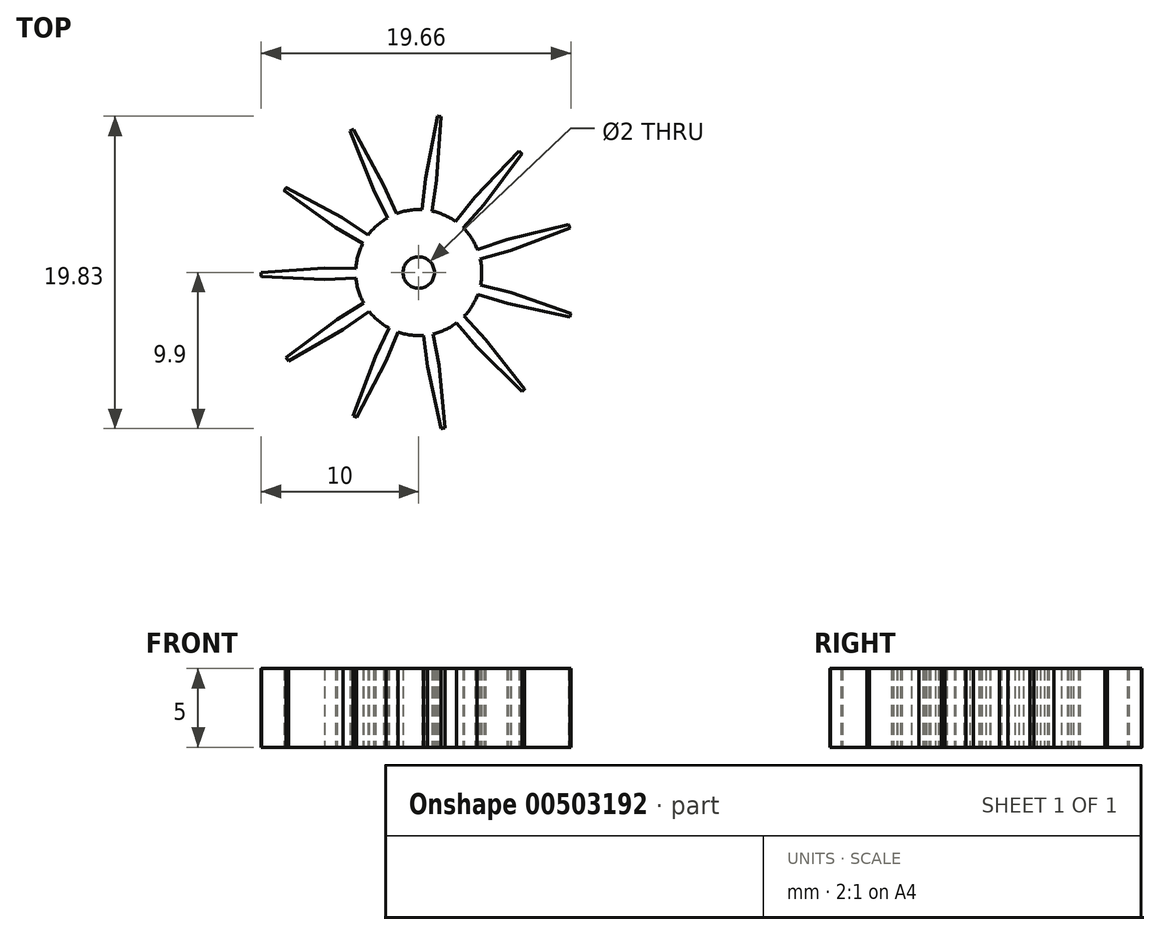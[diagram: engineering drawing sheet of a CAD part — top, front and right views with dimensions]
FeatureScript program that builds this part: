
annotation { "Feature Type Name" : "Feature", "Feature Type Description" : "" }
export const myFeature = defineFeature(function(context is Context, id is Id, definition is map)
    precondition{}
    {
        {
            var Q0;
            Q0=qCreatedBy(makeId("Top.planeOp"),FACE);
            var sketch = newSketch(context, id + "F0", { "sketchPlane" : qUnion([Q0])});
            skCircle(sketch, "E0", {"center": v(0, 0) * mm, "radius": 1 * mm});
            skArc(sketch, "E1", {"start": v(1.14, 5.89) * mm, "mid": v(0.78, 5.95) * mm, "end": v(0.42, 5.99) * mm, "construction": true});
            skArc(sketch, "E2", {"start": v(1.43, 9.9) * mm, "mid": v(1.3, 9.91) * mm, "end": v(1.19, 9.93) * mm});
            skCircle(sketch, "E3", {"center": v(0, 0) * mm, "radius": 4 * mm});
            skLineSegment(sketch, "E4", {"start": v(0, 0) * mm, "end": v(0, 7.63) * mm, "construction": true});
            skLineSegment(sketch, "E5", {"start": v(0, 0) * mm, "end": v(2.03, 7.58) * mm, "construction": true});
            skLineSegment(sketch, "E6", {"start": v(0.42, 5.99) * mm, "end": v(0.2, 4) * mm});
            skLineSegment(sketch, "E7", {"start": v(1.19, 9.93) * mm, "end": v(0.42, 5.99) * mm});
            skLineSegment(sketch, "E8", {"start": v(1.43, 9.9) * mm, "end": v(1.14, 5.89) * mm});
            skLineSegment(sketch, "E9", {"start": v(1.14, 5.89) * mm, "end": v(0.83, 3.91) * mm});
            skLineSegment(sketch, "E10", {"start": v(0.33, 6.33) * mm, "end": v(0, 0) * mm, "construction": true});
            skLineSegment(sketch, "E11", {"start": v(0, 0) * mm, "end": v(1.34, 6.3) * mm, "construction": true});
            skSolve(sketch);
        }
        {
            var Q0;
            Q0=makeQuery(id+"F0.imprint","IMPRINT",FACE,{"disambiguationData":[TD([[makeQuery(id+"F0.imprint","IMPRINT",EDGE,{"derivedFrom":sQuery(id+"F0.wireOp",EDGE,"E0")}),-1.0]])]});
            extrude(context, id + "F1", {"entities" : qUnion([Q0]), "depth" : 5 * mm});
        }
        {
            var Q0;
            Q0=makeQuery(id+"F0.imprint","IMPRINT",FACE,{"disambiguationData":[TD([[makeQuery(id+"F0.imprint","IMPRINT",EDGE,{"derivedFrom":sQuery(id+"F0.wireOp",EDGE,"E2")}),1.0]])]});
            extrude(context, id + "F2", {"entities" : qUnion([Q0]), "depth" : 5 * mm});
        }
        {
            var Q0;
            Q0=makeQuery(id+"F2.opExtrude","SWEPT_BODY",BODY,{"disambiguationData":[OSD([sQuery(id+"F0.wireOp",EDGE,"E2"),sQuery(id+"F0.wireOp",EDGE,"E3"),sQuery(id+"F0.wireOp",EDGE,"E6"),sQuery(id+"F0.wireOp",EDGE,"E7"),sQuery(id+"F0.wireOp",EDGE,"E8"),sQuery(id+"F0.wireOp",EDGE,"E9")])]});
            var Q1;
            Q1=makeQuery(id+"F1.opExtrude","SWEPT_FACE",FACE,{"disambiguationData":[OSD([sQuery(id+"F0.wireOp",EDGE,"E0")])]});
            circularPattern(context, id + "F3", {"operationType" : NewBodyOperationType.ADD, "entities" : qUnion([Q0]), "axis" : qUnion([Q1]), "angle" : 360 * degree, "instanceCount" : 11, "equalSpace" : true});
        }
    });
